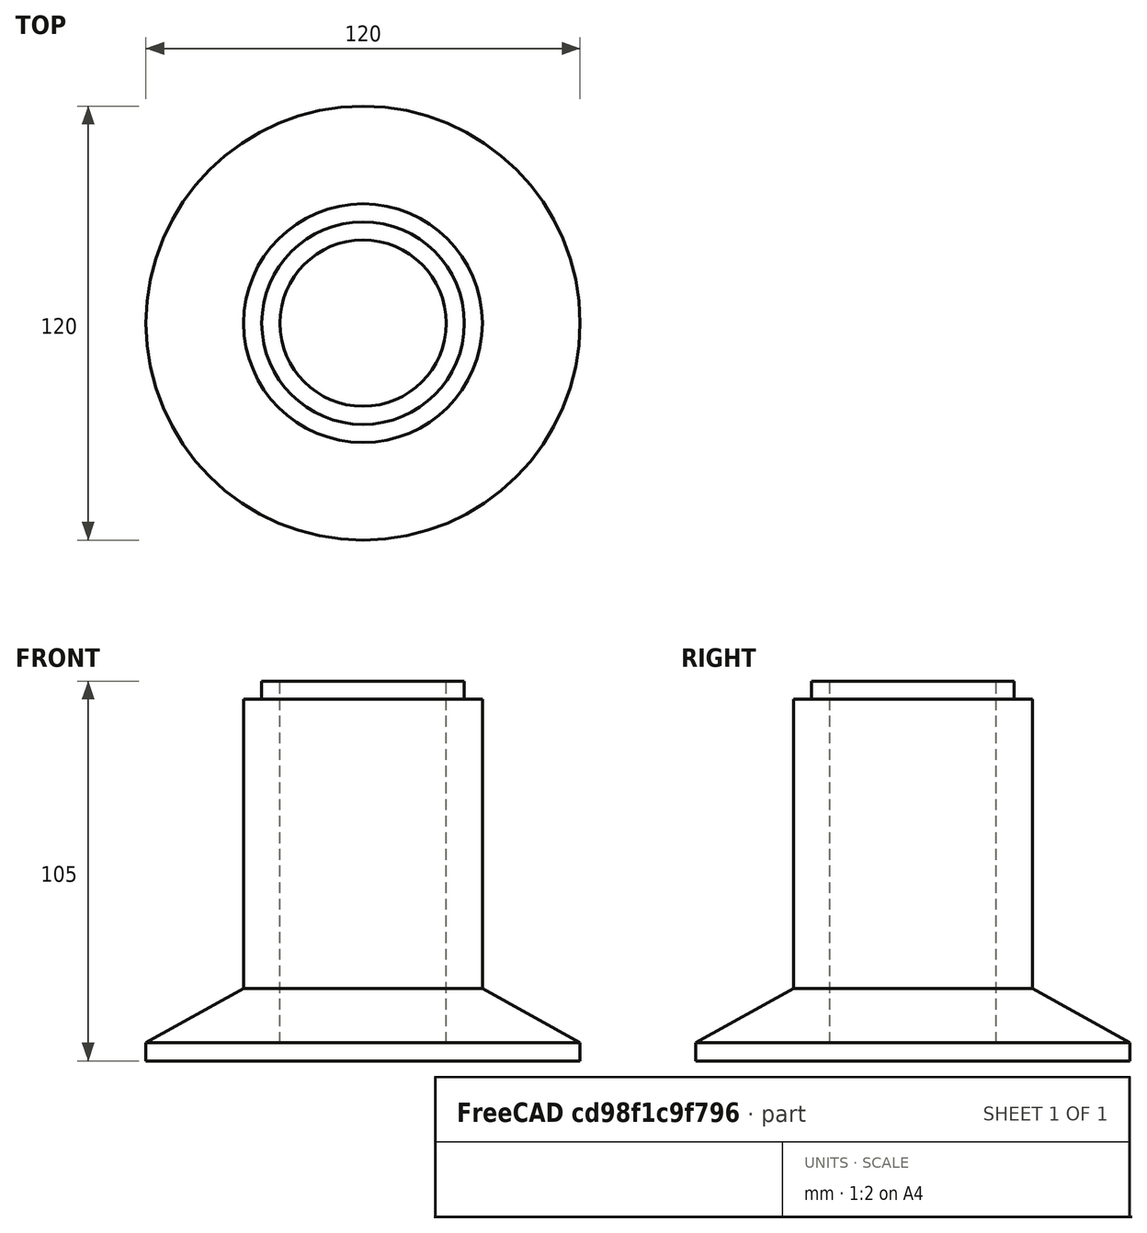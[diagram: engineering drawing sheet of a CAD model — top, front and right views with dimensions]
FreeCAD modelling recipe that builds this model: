
FCSTD DOCUMENT  (FreeCAD 0.20R29410 (Git))
Label: lamp_m14
License: All rights reserved
LicenseURL: http://en.wikipedia.org/wiki/All_rights_reserved
objects: Sketcher::SketchObject×1, PartDesign::Revolution×1, PartDesign::Body×1
note: 4 computed .brp shape members not serialized (recipe doc carries the construction recipe); baked Part::Feature solids carry a one-line shape summary decoded from their .brp

FEATURE [Sketcher::SketchObject] Sketch
  FullyConstrained = true
  MapMode = 5
  Placement = pos=(0,0,0) rot=(1,0,0;1.5708rad)
  Support = -> [XZ_Plane]
  sketch-geometry (10):
    g0: LineSegment StartX=0 StartY=0 StartZ=0 EndX=-60 EndY=0 EndZ=0
    g1: LineSegment StartX=0 StartY=0 StartZ=0 EndX=0 EndY=5 EndZ=0
    g2: LineSegment StartX=0 StartY=5 StartZ=0 EndX=-23 EndY=5 EndZ=0
    g3: LineSegment StartX=-23 StartY=5 StartZ=0 EndX=-23 EndY=105 EndZ=0
    g4: LineSegment StartX=-23 StartY=105 StartZ=0 EndX=-28 EndY=105 EndZ=0
    g5: LineSegment StartX=-28 StartY=105 StartZ=0 EndX=-28 EndY=100 EndZ=0
    g6: LineSegment StartX=-60 StartY=0 StartZ=0 EndX=-60 EndY=5 EndZ=0
    g7: LineSegment StartX=-28 StartY=100 StartZ=0 EndX=-33 EndY=100 EndZ=0
    g8: LineSegment StartX=-33 StartY=20 StartZ=0 EndX=-33 EndY=100 EndZ=0
    g9: LineSegment StartX=-60 StartY=5 StartZ=0 EndX=-33 EndY=20 EndZ=0
  constraints (29):
    c: Coincident(g0,g-1)
    c: Distance(g0) = 60
    c: Coincident(g1,g0)
    c: Parallel(g0,g-1)
    c: Parallel(g1,g-2)
    c: Distance(g1) = 5
    c: Distance(g2) = 23
    c: Parallel(g2,g-1)
    c: Coincident(g2,g1)
    c: Parallel(g3,g-2)
    c: Distance(g3) = 100
    c: Coincident(g3,g2)
    c: Distance(g4) = 5
    c: Parallel(g4,g-1)
    c: Distance(g5) = 5
    c: Parallel(g5,g-2)
    c: Coincident(g5,g4)
    c: Coincident(g4,g3)
    c: Coincident(g6,g0)
    c: Parallel(g6,g-2)
    c: Distance(g6) = 5
    c: Coincident(g7,g5)
    c: Parallel(g7,g-1)
    c: Distance(g7) = 5
    c: Coincident(g8,g7)
    c: Parallel(g8,g3)
    c: Coincident(g9,g6)
    c: Distance(g8) = 80
    c: Coincident(g9,g8)
FEATURE [PartDesign::Revolution] Revolution
  Angle = 360
  Axis = (0,-2e-16,1)
  Base = (0,0,0)
  Placement = pos=(0,0,0) rot=(1,0,0;1.5708rad)
  Profile = -> Sketch
  ReferenceAxis = -> Sketch [V_Axis]
FEATURE [PartDesign::Body] Body
  Group = -> [Sketch,Revolution]
  Origin = -> Origin
  Tip = -> Revolution
